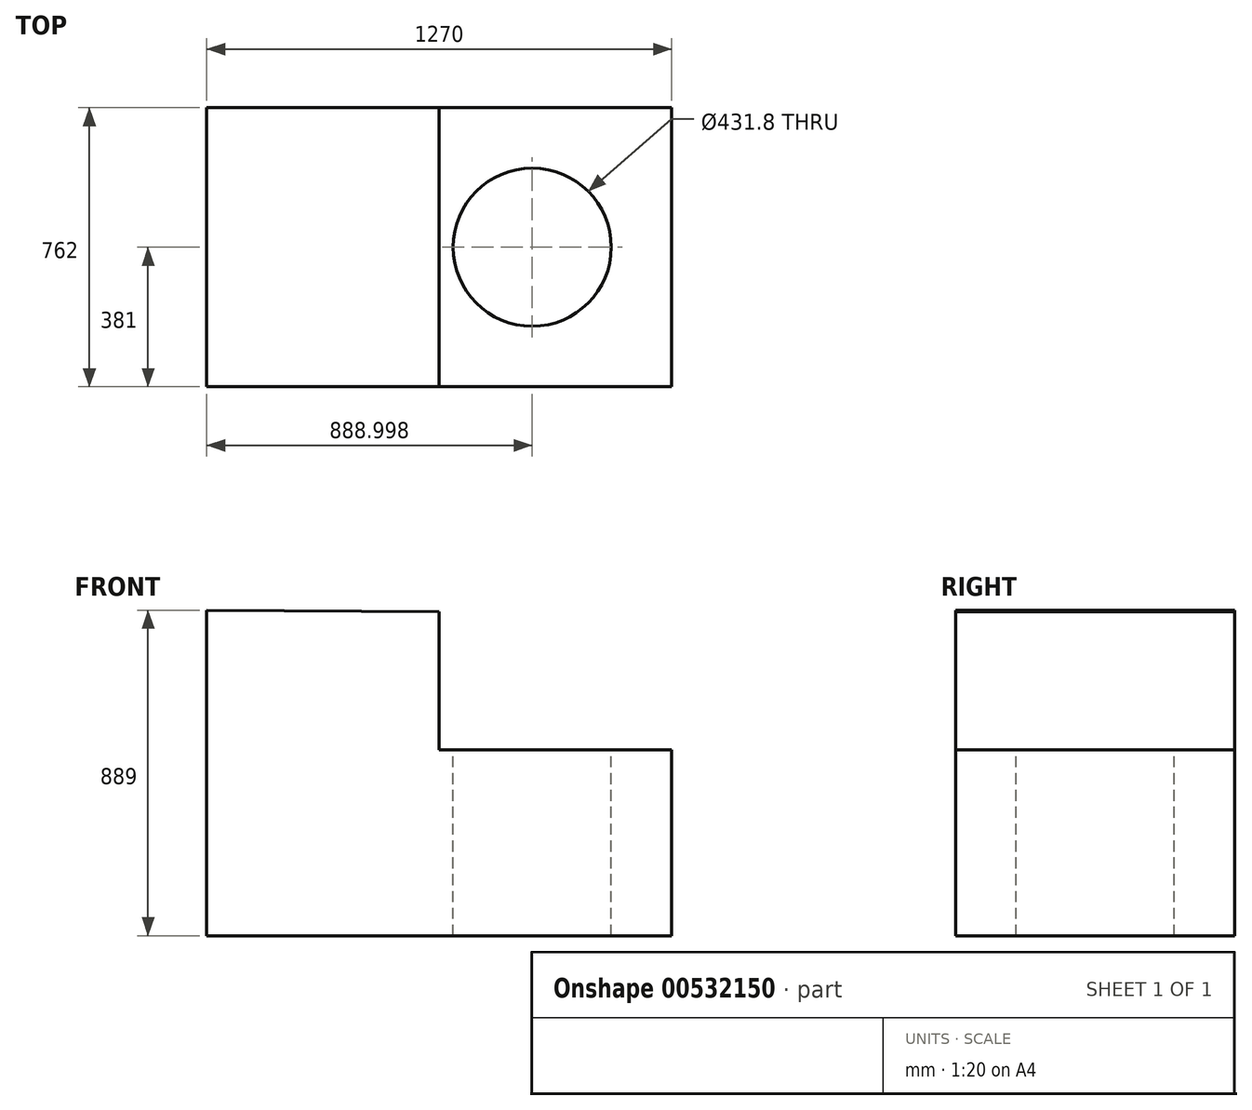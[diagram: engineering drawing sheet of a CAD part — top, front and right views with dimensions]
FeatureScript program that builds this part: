
annotation { "Feature Type Name" : "Feature", "Feature Type Description" : "" }
export const myFeature = defineFeature(function(context is Context, id is Id, definition is map)
    precondition{}
    {
        {
            var Q0;
            Q0=qCreatedBy(makeId("Front.planeOp"),FACE);
            var sketch = newSketch(context, id + "F0", { "sketchPlane" : qUnion([Q0])});
            skPoint(sketch, "E0.middle", {"position": v(0, 0) * mm});
            skLineSegment(sketch, "E1", {"start": v(-55.7, 114.88) * mm, "end": v(-55.7, -774.12) * mm});
            skLineSegment(sketch, "E2", {"start": v(-55.7, -774.12) * mm, "end": v(1214.3, -774.12) * mm});
            skLineSegment(sketch, "E3", {"start": v(1214.3, -774.12) * mm, "end": v(1214.3, -266.12) * mm});
            skLineSegment(sketch, "E4", {"start": v(1214.3, -266.12) * mm, "end": v(579.3, -266.12) * mm});
            skLineSegment(sketch, "E5", {"start": v(579.3, -266.12) * mm, "end": v(579.3, 110.95) * mm});
            skLineSegment(sketch, "E6", {"start": v(579.3, 110.95) * mm, "end": v(-55.7, 114.88) * mm});
            skSolve(sketch);
        }
        {
            var Q0;
            Q0 = qSketchRegion(id + "F0", true);
            extrude(context, id + "F1", {"entities" : qUnion([Q0]), "depth" : 762 * mm, "offsetDistance" : 25.4 * mm});
        }
        {
            var Q0;
            Q0=makeQuery(id+"F1.opExtrude","SWEPT_FACE",FACE,{"disambiguationData":[OSD([sQuery(id+"F0.wireOp",EDGE,"E4")])]});
            var sketch = newSketch(context, id + "F2", { "sketchPlane" : qUnion([Q0])});
            skCircle(sketch, "E7", {"center": v(833.3, -381) * mm, "radius": 215.9 * mm});
            skSolve(sketch);
        }
        {
            var Q0;
            Q0 = qSketchRegion(id + "F2", true);
            extrude(context, id + "F3", {"entities" : qUnion([Q0]), "operationType" : NewBodyOperationType.REMOVE, "endBound" : BoundingType.THROUGH_ALL, "oppositeDirection" : true, "depth" : 25.4 * mm, "offsetDistance" : 25.4 * mm});
        }
    });
